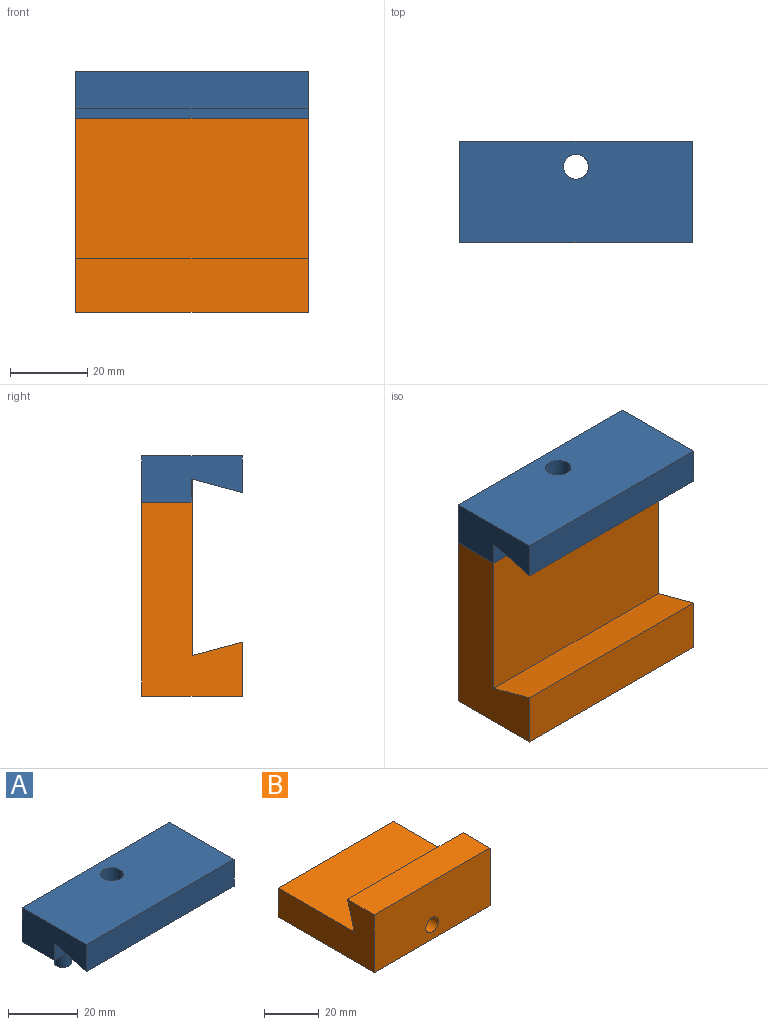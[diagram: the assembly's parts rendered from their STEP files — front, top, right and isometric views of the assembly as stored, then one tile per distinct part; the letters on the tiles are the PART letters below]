
ASSEMBLY  parts=2 mates=1
PART A: 13 faces, bbox 60x26x21 mm
  f0: plane 60x9.48mm, normal (0,-1,0), area 569mm2, adj f2,f3,f4,f6
  f1: plane 60x12mm, normal (0,1,0), area 720mm2, adj f2,f3,f4,f5
  f2: plane 26x12mm, normal (-1,0,0), area 256.6mm2, adj f0,f1,f4,f5,f6,f7
  f3: plane 26x12mm, normal (1,0,0), area 256.6mm2, adj f0,f1,f4,f5,f6,f7
  f4: plane 60x26mm, normal (0,0,1), area 1526.8mm2, adj f0,f1,f2,f3,f8
  f5: plane 60x13mm, normal (0,0,-1), area 709.1mm2, adj f1,f2,f3,f7,f8,f9,f11
  f6: plane 60x13mm, normal (0,0.26,-0.97), area 807.5mm2, adj f0,f2,f3,f7
  f7: plane 60x6mm, normal (0,-1,0), area 360mm2, adj f2,f3,f5,f6
  f8: cylinder r=3.25mm len=12mm, axis (0,0,-1), area 245mm2, adj f4,f5
  f9: cylinder r=2.45mm len=9mm, axis (0,0,1), area 138.5mm2, adj f5,f10
  f10: plane 4.9x4.9mm, normal (0,0,-1), area 18.9mm2, adj f9
  f11: cylinder r=2.45mm len=9mm, axis (0,0,1), area 138.5mm2, adj f5,f12
  f12: plane 4.9x4.9mm, normal (0,0,-1), area 18.9mm2, adj f11
PART B: 13 faces, bbox 60x50x26 mm
  f0: plane 60x13mm, normal (0,1,0), area 707.5mm2, adj f1,f2,f5,f7,f8,f9,f11
  f1: plane 50x26mm, normal (-1,0,0), area 808.6mm2, adj f0,f3,f4,f5,f6,f7
  f2: plane 50x26mm, normal (1,0,0), area 808.6mm2, adj f0,f3,f4,f5,f6,f7
  f3: plane 60x26mm, normal (0,-1,0), area 1526.8mm2, adj f1,f2,f4,f5,f8
  f4: plane 60x13.95mm, normal (0,0,1), area 836.7mm2, adj f1,f2,f3,f6
  f5: plane 60x50mm, normal (0,0,-1), area 3000mm2, adj f0,f1,f2,f3
  f6: plane 60x13mm, normal (0,0.97,-0.26), area 807.5mm2, adj f1,f2,f4,f7
  f7: plane 60x39.54mm, normal (0,0,1), area 2372.3mm2, adj f0,f1,f2,f6
  f8: cylinder r=3.25mm len=50mm, axis (0,1,0), area 1021mm2, adj f0,f3
  f9: cylinder r=2.5mm len=10mm, axis (0,1,0), area 157.1mm2, adj f0,f10
  f10: plane 5x5mm, normal (0,1,0), area 19.6mm2, adj f9
  f11: cylinder r=2.5mm len=10mm, axis (0,1,0), area 157.1mm2, adj f0,f12
  f12: plane 5x5mm, normal (0,1,0), area 19.6mm2, adj f11
PLACE A t=(-12.03,1.53,20.22)mm
PLACE B rot(axis=(1,0,0),90deg) t=(-12.03,1.53,-10.78)mm
MATE fastened B.f0 <-> A.f5  axis (0,0,1) through (-42.03,14.53,14.22)mm
